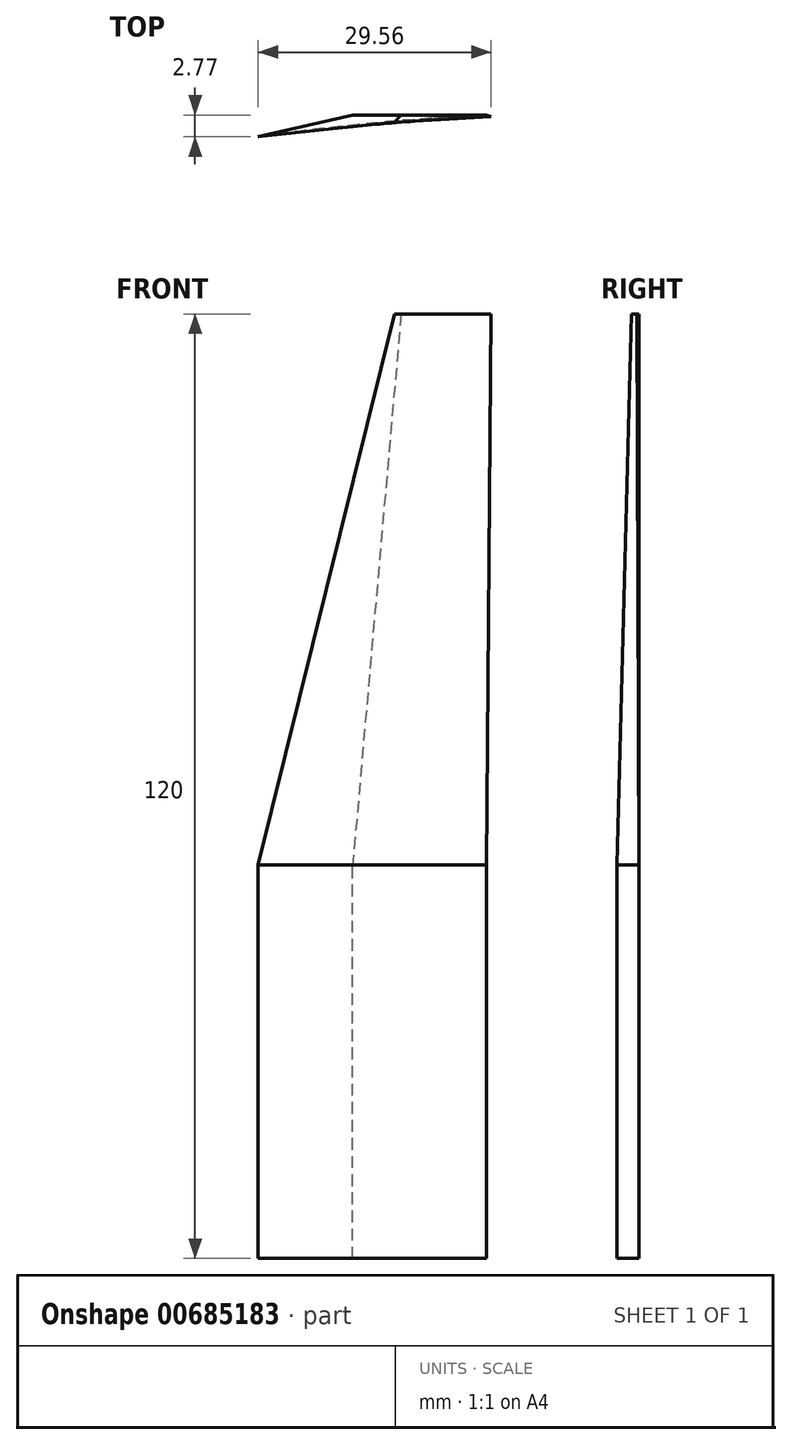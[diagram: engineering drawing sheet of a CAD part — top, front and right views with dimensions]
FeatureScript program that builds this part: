
annotation { "Feature Type Name" : "Feature", "Feature Type Description" : "" }
export const myFeature = defineFeature(function(context is Context, id is Id, definition is map)
    precondition{}
    {
        {
            var Q0;
            Q0=qCreatedBy(makeId("Top.planeOp"),FACE);
            var sketch = newSketch(context, id + "F0", { "sketchPlane" : qUnion([Q0])});
            skLineSegment(sketch, "E0", {"start": v(0, 0) * mm, "end": v(17, 0) * mm});
            skLineSegment(sketch, "E1", {"start": v(-12, -2.77) * mm, "end": v(0, 0) * mm});
            skArc(sketch, "E2", {"start": v(17, 0) * mm, "mid": v(2.47, -1.03) * mm, "end": v(-12, -2.77) * mm});
            skSolve(sketch);
        }
        {
            var Q0;
            Q0=makeQuery(id+"F0.imprint","IMPRINT",FACE,{"disambiguationData":[TD([[makeQuery(id+"F0.imprint","IMPRINT",EDGE,{"derivedFrom":sQuery(id+"F0.wireOp",EDGE,"E0")}),-1.0]])]});
            cPlane(context, id + "F1", {"entities" : qUnion([Q0]), "cplaneType" : CPlaneType.OFFSET, "offset" : 50 * mm, "width" : 150 * mm, "height" : 150 * mm});
        }
        {
            var Q0;
            Q0=qCreatedBy(id+"F1.planeOp",FACE);
            var sketch = newSketch(context, id + "F2", { "sketchPlane" : qUnion([Q0])});
            skLineSegment(sketch, "E3.0", {"start": v(-12, -2.77) * mm, "end": v(0, 0) * mm});
            skArc(sketch, "E4.0", {"start": v(17, 0) * mm, "mid": v(2.47, -1.03) * mm, "end": v(-12, -2.77) * mm});
            skLineSegment(sketch, "E5.0", {"start": v(0, 0) * mm, "end": v(17, 0) * mm});
            skSolve(sketch);
        }
        {
            var Q0;
            Q0=qCreatedBy(id+"F1.planeOp",FACE);
            cPlane(context, id + "F3", {"entities" : qUnion([Q0]), "cplaneType" : CPlaneType.OFFSET, "offset" : 70 * mm, "width" : 150 * mm, "height" : 150 * mm});
        }
        {
            var Q0;
            Q0=qCreatedBy(id+"F3.planeOp",FACE);
            var sketch = newSketch(context, id + "F4", { "sketchPlane" : qUnion([Q0])});
            skLineSegment(sketch, "E6", {"start": v(17.56, -0.22) * mm, "end": v(6.14, 0) * mm});
            skLineSegment(sketch, "E7", {"start": v(6.14, 0) * mm, "end": v(5.29, -0.9) * mm});
            skLineSegment(sketch, "E8", {"start": v(5.29, -0.9) * mm, "end": v(17.56, -0.22) * mm});
            skSolve(sketch);
        }
        {
            var Q0;
            Q0=makeQuery(id+"F0.imprint","IMPRINT",FACE,{"disambiguationData":[TD([[makeQuery(id+"F0.imprint","IMPRINT",EDGE,{"derivedFrom":sQuery(id+"F0.wireOp",EDGE,"E0")}),-1.0]])]});
            var Q1;
            Q1=makeQuery(id+"F2.imprint","IMPRINT",FACE,{"disambiguationData":[TD([[makeQuery(id+"F2.imprint","IMPRINT",EDGE,{"derivedFrom":sQuery(id+"F2.wireOp",EDGE,"E3.0")}),-1.0]])]});
            loft(context, id + "F5", {"sheetProfilesArray" : [{ "sheetProfileEntities" : qUnion([Q0]) }, { "sheetProfileEntities" : qUnion([Q1]) }]});
        }
        {
            var Q1;
            Q1=makeQuery(id+"F4.imprint","IMPRINT",FACE,{"disambiguationData":[TD([[makeQuery(id+"F4.imprint","IMPRINT",EDGE,{"derivedFrom":sQuery(id+"F4.wireOp",EDGE,"E6")}),1.0]])]});
            var Q2;
            Q2=makeQuery(id+"F2.imprint","IMPRINT",FACE,{"disambiguationData":[TD([[makeQuery(id+"F2.imprint","IMPRINT",EDGE,{"derivedFrom":sQuery(id+"F2.wireOp",EDGE,"E3.0")}),-1.0]])]});
            loft(context, id + "F6", {"operationType" : NewBodyOperationType.ADD, "sheetProfilesArray" : [{ "sheetProfileEntities" : qUnion([Q1]) }, { "sheetProfileEntities" : qUnion([Q2]) }]});
        }
    });
